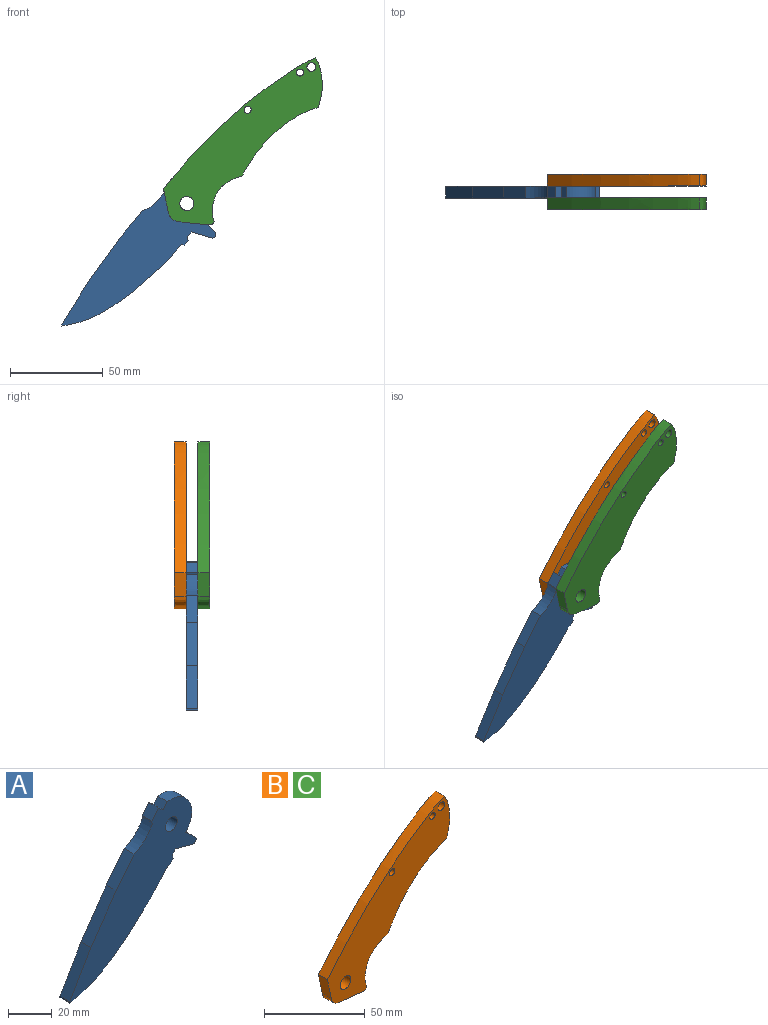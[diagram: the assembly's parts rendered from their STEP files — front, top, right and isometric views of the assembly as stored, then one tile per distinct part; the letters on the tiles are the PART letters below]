
ASSEMBLY  parts=3 mates=2
PART A: 22 faces, bbox 82x6.4x81.5 mm
  f0: cylinder r=21.5mm len=12.02mm, axis (0,-1,0), area 108mm2, adj f1,f18,f19,f20
  f1: plane 14.81x11.57mm, normal (-0.79,0,0.62), area 119.4mm2, adj f0,f2,f19,f20
  f2: plane 23.84x16.38mm, normal (-0.82,0,0.57), area 183.6mm2, adj f1,f3,f19,f20
  f3: plane 23.52x13.78mm, normal (-0.86,0,0.51), area 173.1mm2, adj f2,f4,f19,f20
  f4: plane 6.35x0.71mm, normal (-1,0,0), area 4.5mm2, adj f3,f5,f19,f20
  f5: extruded ~63.51x45.22mm, area 505.5mm2, adj f4,f6,f19,f20
  f6: plane 6.35x1.47mm, normal (0,0,-1), area 9.3mm2, adj f5,f7,f19,f20
  f7: plane 6.35x2.65mm, normal (0.79,0,-0.61), area 21.3mm2, adj f6,f8,f19,f20
  f8: plane 6.35x2.21mm, normal (0.97,0,0.24), area 14.4mm2, adj f7,f9,f19,f20
  f9: plane 6.35x2.26mm, normal (0.74,0,-0.67), area 19.4mm2, adj f8,f10,f19,f20
  f10: plane 11.18x6.35mm, normal (-0.25,0,-0.97), area 73.4mm2, adj f9,f11,f19,f20
  f11: cylinder r=1.79mm len=6.35mm, axis (0,-1,0), area 28.4mm2, adj f10,f12,f19,f20
  f12: plane 6.35x3.83mm, normal (0.71,0,0.71), area 34.4mm2, adj f11,f13,f19,f20
  f13: plane 6.35x2.67mm, normal (0.66,0,0.75), area 22.7mm2, adj f12,f14,f19,f20
  f14: cylinder r=13.47mm len=23.11mm, axis (0,-1,0), area 217.1mm2, adj f13,f15,f19,f20
  f15: plane 6.35x3.23mm, normal (-0.77,0,0.63), area 26.5mm2, adj f14,f16,f19,f20
  f16: plane 6.35x3.24mm, normal (0.63,0,0.77), area 26.6mm2, adj f15,f17,f19,f20
  f17: plane 6.35x5.21mm, normal (-0.77,0,0.63), area 42.7mm2, adj f16,f18,f19,f20
  f18: plane 6.35x1.27mm, normal (-0.94,0,-0.34), area 8.6mm2, adj f0,f17,f19,f20
  f19: plane 81.99x81.54mm, normal (0,1,0), area 2299.9mm2, adj f0,f1,f2,f3,f4,f5,f6,f7
  f20: plane 81.99x81.54mm, normal (0,-1,0), area 2299.9mm2, adj f0,f1,f2,f3,f4,f5,f6,f7
  f21: cylinder r=3.81mm len=7.62mm, axis (0,1,0), area 152mm2, adj f19,f20
PART B: 12 faces, bbox 85.8x6.4x90.2 mm
  f0: extruded ~26.62x6.35mm, area 175mm2, adj f1,f5,f6,f7
  f1: extruded ~81.99x70.49mm, area 692.1mm2, adj f0,f2,f6,f7
  f2: plane 12.7x6.35mm, normal (-0.98,0,-0.21), area 82.5mm2, adj f1,f3,f6,f7
  f3: extruded ~24.69x6.84mm, area 179.8mm2, adj f2,f4,f6,f7
  f4: extruded ~24.51x16.04mm, area 207.3mm2, adj f3,f5,f6,f7
  f5: extruded ~41.15x37.06mm, area 361.2mm2, adj f0,f4,f6,f7
  f6: plane 90.19x85.8mm, normal (0,-1,0), area 2533.6mm2, adj f0,f1,f2,f3,f4,f5,f8,f9
  f7: plane 90.19x85.8mm, normal (0,1,0), area 2533.6mm2, adj f0,f1,f2,f3,f4,f5,f8,f9
  f8: cylinder r=3.81mm len=7.62mm, axis (0,1,0), area 152mm2, adj f6,f7
  f9: cylinder r=1.91mm len=6.35mm, axis (0,1,0), area 76mm2, adj f6,f7
  f10: cylinder r=1.91mm len=6.35mm, axis (0,1,0), area 76mm2, adj f6,f7
  f11: cylinder r=2.37mm len=6.35mm, axis (0,1,0), area 94.5mm2, adj f6,f7
PART C: same geometry as B
PLACE A rot(axis=(0,1,0),1.3deg) t=(-22.88,16.58,-5.16)mm
PLACE B t=(-23.03,29.28,-4.94)mm
PLACE C t=(-23.03,16.58,-4.94)mm fixed
MATE fastened B.f8 <-> C.f8  axis (0,-1,0) through (-32.23,22.93,-11.56)mm
MATE revolute A.f21 <-> C.f8  axis (0,-1,0) through (-32.23,16.58,-11.56)mm
